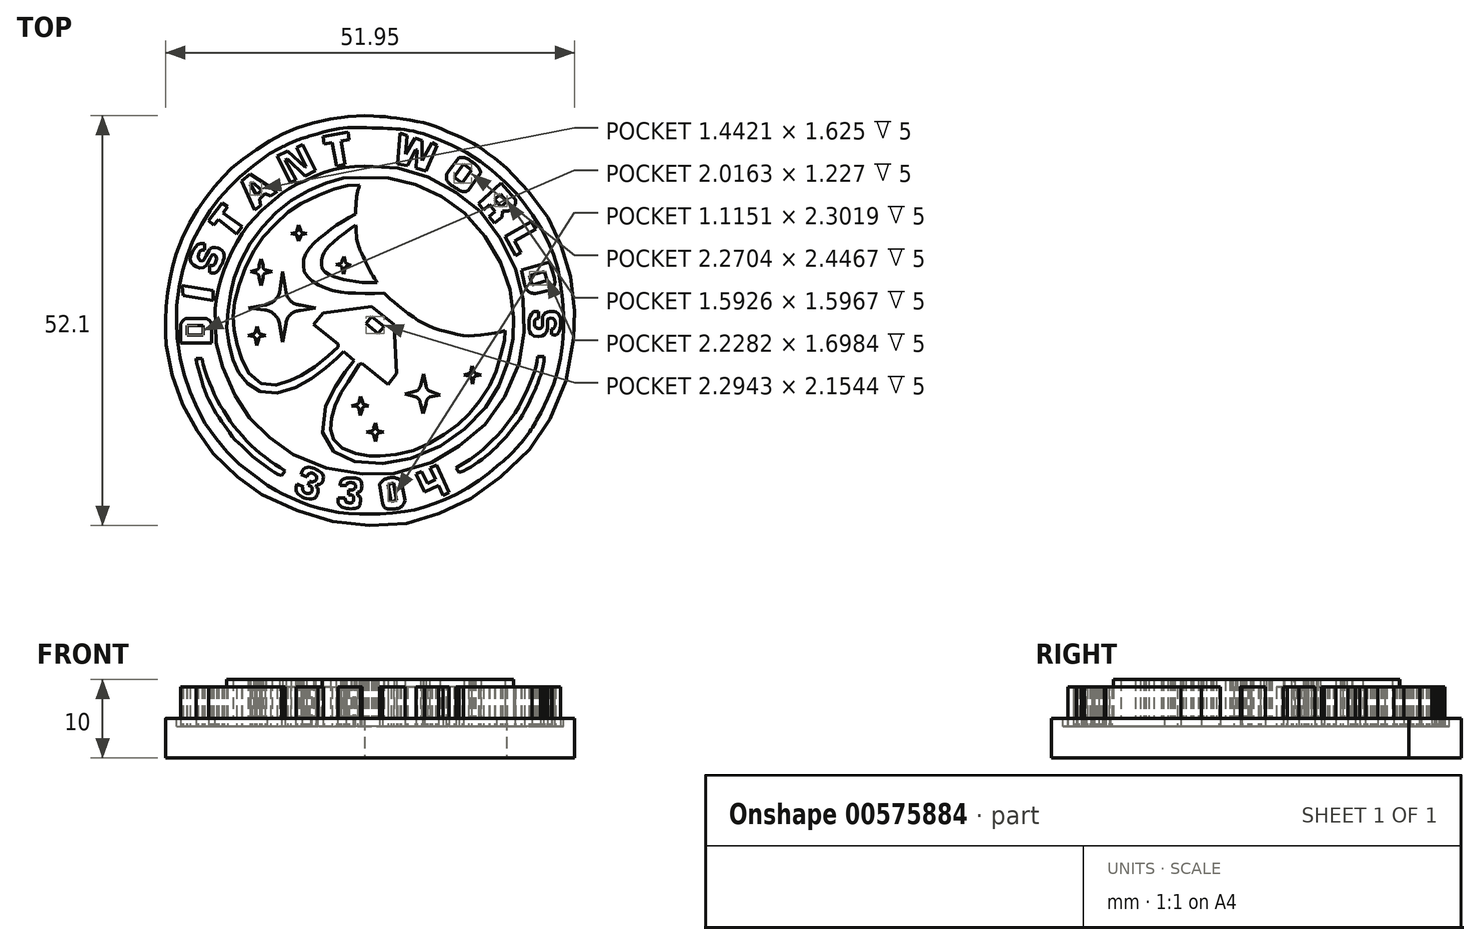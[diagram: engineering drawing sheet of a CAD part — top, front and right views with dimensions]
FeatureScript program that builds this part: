
annotation { "Feature Type Name" : "Feature", "Feature Type Description" : "" }
export const myFeature = defineFeature(function(context is Context, id is Id, definition is map)
    precondition{}
    {
        {
            var Q0;
            Q0=qCreatedBy(makeId("Top.planeOp"),FACE);
            var sketch = newSketch(context, id + "F0", { "sketchPlane" : qUnion([Q0])});
            skFitSpline(sketch, "E0", {"points": [v(33.66, 54.7) * mm, v(28.64, 54.13) * mm, v(24.15, 52.76) * mm, v(20.9, 51.03) * mm, v(17.39, 48.57) * mm, v(15.5, 46.67) * mm, v(13.56, 44.31) * mm, v(11.47, 41.1) * mm, v(9.64, 36.9) * mm, v(9.01, 34.3) * mm, v(8.48, 31.08) * mm, v(8.38, 27.96) * mm, v(8.48, 25.57) * mm], "startDerivative": vector(-44.63, -0.28) * mm, "endDerivative": vector(4.64, -29.37) * mm});
            skFitSpline(sketch, "E1", {"points": [v(8.48, 25.57) * mm, v(9.04, 22.5) * mm, v(9.97, 19.28) * mm, v(11.27, 16.56) * mm, v(12.7, 14.13) * mm, v(14.12, 12.14) * mm, v(16.89, 9.38) * mm, v(19.17, 7.53) * mm, v(22.3, 5.7) * mm, v(27.48, 3.7) * mm, v(31.2, 2.9) * mm, v(36.42, 2.6) * mm, v(40.28, 3.17) * mm, v(43.93, 4.47) * mm, v(47.72, 6.36) * mm, v(51.35, 9.16) * mm, v(55.07, 12.81) * mm, v(57.46, 16.57) * mm, v(59.59, 22.19) * mm, v(60.29, 27.4) * mm, v(60.32, 29.57) * mm, v(59.95, 33.52) * mm, v(59.06, 36.85) * mm, v(57.9, 40.04) * mm, v(56.33, 42.66) * mm, v(54.07, 45.62) * mm, v(51.71, 48.05) * mm], "startDerivative": vector(14.51, -87.06) * mm, "endDerivative": vector(-72.64, 61.42) * mm});
            skFitSpline(sketch, "E2", {"points": [v(51.71, 48.05) * mm, v(48.99, 50.18) * mm, v(47.02, 51.4) * mm, v(44.2, 52.67) * mm, v(41.74, 53.63) * mm, v(38.88, 54.2) * mm, v(36.42, 54.53) * mm, v(33.66, 54.7) * mm], "startDerivative": vector(-17.82, 14.28) * mm, "endDerivative": vector(-30.74, 1.43) * mm});
            skSolve(sketch);
        }
        {
            var Q0;
            Q0 = qSketchRegion(id + "F0", true);
            extrude(context, id + "F1", {"entities" : qUnion([Q0]), "depth" : 5 * mm, "offsetDistance" : 25 * mm});
        }
        {
            var Q0;
            Q0=makeQuery(id+"F1.opExtrude","CAP_FACE",FACE,{"disambiguationData":[OSD([sQuery(id+"F0.wireOp",EDGE,"E0"),sQuery(id+"F0.wireOp",EDGE,"E1"),sQuery(id+"F0.wireOp",EDGE,"E2")])],"isStart":false});
            var sketch = newSketch(context, id + "F2", { "sketchPlane" : qUnion([Q0])});
            skFitSpline(sketch, "E3", {"points": [v(26.87, 52.15) * mm, v(24.92, 51.5) * mm, v(23.24, 50.73) * mm, v(21.37, 49.7) * mm], "startDerivative": vector(-6, -1.7) * mm, "endDerivative": vector(-5.43, -3.28) * mm});
            skFitSpline(sketch, "E4", {"points": [v(21.37, 49.7) * mm, v(20.03, 48.73) * mm, v(18.51, 47.52) * mm, v(17.4, 46.52) * mm, v(16.7, 45.8) * mm, v(15.56, 44.58) * mm, v(14.8, 43.75) * mm, v(14.16, 42.85) * mm, v(13.55, 41.87) * mm, v(12.56, 40.19) * mm, v(11.73, 38.52) * mm, v(11.22, 37.14) * mm, v(10.85, 35.97) * mm, v(10.46, 34.7) * mm, v(10.18, 33.2) * mm, v(9.83, 31.07) * mm, v(9.81, 29.8) * mm, v(9.79, 28.26) * mm, v(9.83, 26.76) * mm, v(10.11, 24.62) * mm, v(10.52, 22.74) * mm, v(10.87, 21.34) * mm, v(11.56, 19.44) * mm, v(12.34, 17.62) * mm, v(12.97, 16.39) * mm, v(13.92, 14.83) * mm, v(15.02, 13.43) * mm, v(16.07, 12.14) * mm, v(17.25, 10.88) * mm, v(18.36, 9.98) * mm, v(19.84, 8.78) * mm, v(21.37, 7.7) * mm], "startDerivative": vector(-43.18, -27.56) * mm, "endDerivative": vector(47.9, -24.44) * mm});
            skFitSpline(sketch, "E5", {"points": [v(21.37, 7.7) * mm, v(22.62, 6.94) * mm, v(23.33, 6.6) * mm, v(24.66, 6) * mm, v(26.33, 5.3) * mm, v(27.53, 4.89) * mm, v(29.48, 4.45) * mm, v(30.91, 4.22) * mm, v(32.77, 4.13) * mm, v(34.37, 4.1) * mm, v(36.53, 4.14) * mm, v(38.97, 4.43) * mm, v(40.53, 4.74) * mm, v(42.3, 5.3) * mm, v(44.22, 6.09) * mm, v(46.5, 7.23) * mm, v(49.04, 8.94) * mm, v(50.5, 10.16) * mm], "startDerivative": vector(25.71, -16.24) * mm, "endDerivative": vector(21.37, 21.4) * mm});
            skFitSpline(sketch, "E6", {"points": [v(50.5, 10.16) * mm, v(52.82, 12.29) * mm, v(54.13, 13.87) * mm, v(55.07, 15.18) * mm, v(56.1, 17.01) * mm], "startDerivative": vector(8.33, 7.24) * mm, "endDerivative": vector(4.94, 7.57) * mm});
            skFitSpline(sketch, "E7", {"points": [v(56.1, 17.01) * mm, v(57.07, 19.1) * mm, v(57.9, 21.27) * mm, v(58.38, 23.01) * mm, v(58.74, 25.12) * mm, v(58.9, 27.05) * mm, v(58.96, 29.28) * mm, v(58.76, 31.76) * mm, v(58.42, 34.2) * mm, v(57.83, 36.57) * mm, v(57.05, 38.48) * mm, v(56.1, 40.32) * mm, v(54.62, 42.64) * mm, v(53.36, 44.28) * mm, v(52.3, 45.5) * mm, v(49.9, 47.68) * mm, v(48.22, 48.99) * mm, v(45.67, 50.48) * mm, v(43.38, 51.55) * mm, v(41.07, 52.42) * mm], "startDerivative": vector(18.57, 39) * mm, "endDerivative": vector(-43.4, 12.3) * mm});
            skFitSpline(sketch, "E8", {"points": [v(41.07, 52.42) * mm, v(39.18, 52.84) * mm, v(37.64, 53) * mm, v(35.9, 53.11) * mm, v(33.42, 53.15) * mm, v(31.55, 53.15) * mm, v(29.82, 52.95) * mm, v(26.87, 52.15) * mm], "startDerivative": vector(-13.88, 3.44) * mm, "endDerivative": vector(-17.96, -5.4) * mm});
            skFitSpline(sketch, "E9", {"points": [v(33.66, 48.3) * mm, v(30.82, 48.08) * mm, v(27.92, 47.23) * mm, v(25.62, 46.22) * mm, v(23.66, 45.18) * mm, v(22.01, 43.86) * mm, v(20.42, 42.46) * mm, v(18.59, 40.38) * mm, v(17.12, 38.06) * mm, v(15.96, 35.52) * mm, v(15.16, 33.13) * mm, v(14.7, 30.17) * mm], "startDerivative": vector(-29.66, -0.71) * mm, "endDerivative": vector(-1.88, -34.71) * mm});
            skFitSpline(sketch, "E10", {"points": [v(14.7, 30.17) * mm, v(14.7, 26.26) * mm, v(15.2, 24.08) * mm, v(15.8, 22.28) * mm, v(17.12, 19.38) * mm, v(18.2, 17.48) * mm, v(19.75, 15.5) * mm, v(21.46, 13.94) * mm, v(23.39, 12.32) * mm, v(26.35, 10.85) * mm, v(30.66, 9.41) * mm, v(34.55, 9.14) * mm, v(37.51, 9.23) * mm, v(42.25, 10.66) * mm, v(44.97, 12.22) * mm, v(47.78, 14.33) * mm, v(50.29, 17) * mm, v(52.03, 20.2) * mm, v(53.53, 24.12) * mm, v(53.93, 27.14) * mm, v(53.9, 30.72) * mm, v(53.35, 33.47) * mm, v(52.19, 36.83) * mm, v(50.29, 40.04) * mm, v(48.24, 42.61) * mm, v(45.89, 44.5) * mm, v(43.32, 46.16) * mm, v(40.14, 47.5) * mm, v(37.33, 48.11) * mm, v(33.66, 48.3) * mm], "startDerivative": vector(-5, -110.22) * mm, "endDerivative": vector(-103.89, 2.26) * mm});
            skSolve(sketch);
        }
        {
            var Q0;
            Q0 = qSketchRegion(id + "F2", true);
            extrude(context, id + "F3", {"entities" : qUnion([Q0]), "operationType" : NewBodyOperationType.REMOVE, "oppositeDirection" : true, "depth" : 1 * mm, "offsetDistance" : 25 * mm});
        }
        {
            var Q0;
            Q0=makeQuery(id+"F3.boolean.opBoolean","COPY",FACE,{"derivedFrom":makeQuery(id+"F3.opExtrude","CAP_FACE",FACE,{"disambiguationData":[OSD([sQuery(id+"F2.wireOp",EDGE,"E3"),sQuery(id+"F2.wireOp",EDGE,"E4"),sQuery(id+"F2.wireOp",EDGE,"E5"),sQuery(id+"F2.wireOp",EDGE,"E6"),sQuery(id+"F2.wireOp",EDGE,"E7"),sQuery(id+"F2.wireOp",EDGE,"E8"),sQuery(id+"F2.wireOp",EDGE,"E9"),sQuery(id+"F2.wireOp",EDGE,"E10")])],"isStart":false})});
            var sketch = newSketch(context, id + "F4", { "sketchPlane" : qUnion([Q0])});
            skLineSegment(sketch, "E11", {"start": v(31.56, 52.63) * mm, "end": v(28.37, 52.04) * mm});
            skLineSegment(sketch, "E12", {"start": v(28.37, 52.04) * mm, "end": v(28.54, 51.1) * mm});
            skLineSegment(sketch, "E13", {"start": v(28.54, 51.1) * mm, "end": v(29.55, 51.28) * mm});
            skLineSegment(sketch, "E14", {"start": v(29.55, 51.28) * mm, "end": v(30.1, 48.3) * mm});
            skLineSegment(sketch, "E15", {"start": v(30.1, 48.3) * mm, "end": v(31.2, 48.5) * mm});
            skLineSegment(sketch, "E16", {"start": v(31.2, 48.5) * mm, "end": v(30.66, 51.48) * mm});
            skLineSegment(sketch, "E17", {"start": v(30.66, 51.48) * mm, "end": v(31.7, 51.67) * mm});
            skLineSegment(sketch, "E18", {"start": v(31.56, 52.63) * mm, "end": v(31.7, 51.67) * mm});
            skLineSegment(sketch, "E19", {"start": v(24.95, 46.52) * mm, "end": v(24.28, 46.17) * mm});
            skLineSegment(sketch, "E20", {"start": v(24.28, 46.17) * mm, "end": v(22.54, 49.54) * mm});
            skLineSegment(sketch, "E21", {"start": v(22.54, 49.54) * mm, "end": v(23.85, 50.21) * mm});
            skLineSegment(sketch, "E22", {"start": v(23.85, 50.21) * mm, "end": v(26.08, 48.14) * mm});
            skLineSegment(sketch, "E23", {"start": v(26.25, 48.24) * mm, "end": v(25.03, 50.62) * mm});
            skLineSegment(sketch, "E24", {"start": v(25.03, 50.62) * mm, "end": v(25.78, 51) * mm});
            skLineSegment(sketch, "E25", {"start": v(25.78, 51) * mm, "end": v(27.46, 47.73) * mm});
            skLineSegment(sketch, "E26", {"start": v(27.46, 47.73) * mm, "end": v(26.08, 47.02) * mm});
            skLineSegment(sketch, "E27", {"start": v(26.08, 47.02) * mm, "end": v(23.86, 49.15) * mm});
            skLineSegment(sketch, "E28", {"start": v(23.6, 49.03) * mm, "end": v(24.95, 46.52) * mm});
            skLineSegment(sketch, "E29", {"start": v(23.86, 49.15) * mm, "end": v(23.6, 49.03) * mm});
            skLineSegment(sketch, "E30", {"start": v(26.25, 48.24) * mm, "end": v(26.08, 48.14) * mm});
            skLineSegment(sketch, "E31", {"start": v(19.12, 47.29) * mm, "end": v(18.07, 46.38) * mm});
            skLineSegment(sketch, "E32", {"start": v(18.07, 46.38) * mm, "end": v(19.66, 42.68) * mm});
            skLineSegment(sketch, "E33", {"start": v(19.66, 42.68) * mm, "end": v(20.48, 43.28) * mm});
            skLineSegment(sketch, "E34", {"start": v(20.48, 43.28) * mm, "end": v(20.32, 44.1) * mm});
            skLineSegment(sketch, "E35", {"start": v(20.32, 44.1) * mm, "end": v(21.02, 44.79) * mm});
            skLineSegment(sketch, "E36", {"start": v(21.02, 44.79) * mm, "end": v(21.74, 44.5) * mm});
            skLineSegment(sketch, "E37", {"start": v(21.74, 44.5) * mm, "end": v(22.53, 45.06) * mm});
            skLineSegment(sketch, "E38", {"start": v(22.53, 45.06) * mm, "end": v(19.12, 47.29) * mm});
            skLineSegment(sketch, "E39", {"start": v(19.36, 46.25) * mm, "end": v(20.56, 45.26) * mm});
            skLineSegment(sketch, "E40", {"start": v(20.56, 45.26) * mm, "end": v(19.92, 44.63) * mm});
            skLineSegment(sketch, "E41", {"start": v(19.92, 44.63) * mm, "end": v(19.12, 46) * mm});
            skLineSegment(sketch, "E42", {"start": v(19.36, 46.25) * mm, "end": v(19.12, 46) * mm});
            skLineSegment(sketch, "E43", {"start": v(15.57, 43.62) * mm, "end": v(13.85, 41.36) * mm});
            skLineSegment(sketch, "E44", {"start": v(13.85, 41.36) * mm, "end": v(14.46, 40.8) * mm});
            skLineSegment(sketch, "E45", {"start": v(14.46, 40.8) * mm, "end": v(15.1, 41.5) * mm});
            skLineSegment(sketch, "E46", {"start": v(15.1, 41.5) * mm, "end": v(17.38, 39.67) * mm});
            skLineSegment(sketch, "E47", {"start": v(17.38, 39.67) * mm, "end": v(18.12, 40.58) * mm});
            skLineSegment(sketch, "E48", {"start": v(18.12, 40.58) * mm, "end": v(15.67, 42.33) * mm});
            skLineSegment(sketch, "E49", {"start": v(15.57, 43.62) * mm, "end": v(16.23, 43.11) * mm});
            skLineSegment(sketch, "E50", {"start": v(16.23, 43.11) * mm, "end": v(15.67, 42.33) * mm});
            skFitSpline(sketch, "E51", {"points": [v(13.33, 38.46) * mm, v(12.7, 38.42) * mm, v(12.38, 38.23) * mm, v(12.09, 37.85) * mm, v(11.83, 37.44) * mm, v(11.6, 36.9) * mm, v(11.52, 36.37) * mm, v(11.65, 36.02) * mm, v(11.97, 35.68) * mm, v(12.4, 35.45) * mm, v(13, 35.3) * mm, v(13.61, 35.76) * mm, v(13.95, 36.3) * mm, v(14.2, 36.9) * mm, v(14.4, 37.03) * mm, v(14.65, 37) * mm, v(14.87, 36.74) * mm, v(14.86, 36.43) * mm, v(14.73, 36.01) * mm, v(14.56, 35.74) * mm, v(14.33, 35.65) * mm, v(13.98, 35.65) * mm], "startDerivative": vector(-10.58, 1.4) * mm, "endDerivative": vector(-5.63, -0.2) * mm});
            skLineSegment(sketch, "E52", {"start": v(13.98, 35.65) * mm, "end": v(13.98, 34.78) * mm});
            skLineSegment(sketch, "E53", {"start": v(13.33, 38.46) * mm, "end": v(13.33, 37.64) * mm});
            skFitSpline(sketch, "E54", {"points": [v(13.98, 34.78) * mm, v(14.78, 34.78) * mm, v(15.3, 35.41) * mm, v(15.46, 35.71) * mm, v(15.71, 36.3) * mm], "startDerivative": vector(2.67, -0.65) * mm, "endDerivative": vector(0.47, 2.65) * mm});
            skFitSpline(sketch, "E55", {"points": [v(15.71, 36.3) * mm, v(15.83, 36.86) * mm, v(15.71, 37.44) * mm, v(15.3, 37.76) * mm, v(14.8, 37.92) * mm, v(14.2, 37.9) * mm, v(13.88, 37.55) * mm, v(13.58, 36.97) * mm, v(13.38, 36.57) * mm, v(13.13, 36.27) * mm, v(12.77, 36.3) * mm, v(12.58, 36.6) * mm, v(12.54, 36.98) * mm, v(12.69, 37.4) * mm, v(12.91, 37.57) * mm, v(13.33, 37.64) * mm], "startDerivative": vector(3.34, 6.88) * mm, "endDerivative": vector(6.34, 0.42) * mm});
            skLineSegment(sketch, "E56", {"start": v(10.48, 33.1) * mm, "end": v(14.43, 32.49) * mm});
            skLineSegment(sketch, "E57", {"start": v(14.43, 32.49) * mm, "end": v(14.43, 31.22) * mm});
            skLineSegment(sketch, "E58", {"start": v(14.43, 31.22) * mm, "end": v(10.59, 31.85) * mm});
            skLineSegment(sketch, "E59", {"start": v(10.59, 31.85) * mm, "end": v(10.48, 33.1) * mm});
            skLineSegment(sketch, "E60", {"start": v(10.28, 25.8) * mm, "end": v(14.25, 25.8) * mm});
            skLineSegment(sketch, "E61", {"start": v(14.25, 25.8) * mm, "end": v(14.25, 28) * mm});
            skLineSegment(sketch, "E62", {"start": v(10.28, 25.8) * mm, "end": v(10.28, 28) * mm});
            skLineSegment(sketch, "E63", {"start": v(11.02, 28.95) * mm, "end": v(13.27, 28.95) * mm});
            skFitSpline(sketch, "E64", {"points": [v(11.02, 28.95) * mm, v(10.78, 28.82) * mm, v(10.57, 28.64) * mm, v(10.41, 28.43) * mm, v(10.32, 28.24) * mm, v(10.28, 28) * mm], "startDerivative": vector(-1.22, -0.54) * mm, "endDerivative": vector(-0.17, -1.31) * mm});
            skFitSpline(sketch, "E65", {"points": [v(13.27, 28.95) * mm, v(13.56, 28.9) * mm, v(13.8, 28.8) * mm, v(14.05, 28.58) * mm, v(14.2, 28.27) * mm, v(14.25, 28) * mm], "startDerivative": vector(1.5, -0.14) * mm, "endDerivative": vector(0.37, -1.17) * mm});
            skLineSegment(sketch, "E66", {"start": v(11.14, 28.04) * mm, "end": v(13.16, 28.04) * mm});
            skLineSegment(sketch, "E67", {"start": v(13.16, 28.04) * mm, "end": v(13.16, 26.81) * mm});
            skLineSegment(sketch, "E68", {"start": v(13.16, 26.81) * mm, "end": v(11.14, 26.81) * mm});
            skLineSegment(sketch, "E69", {"start": v(11.14, 26.81) * mm, "end": v(11.14, 28.04) * mm});
            skLineSegment(sketch, "E70", {"start": v(12.26, 23.87) * mm, "end": v(13.03, 23.87) * mm});
            skLineSegment(sketch, "E71", {"start": v(23.55, 9.56) * mm, "end": v(23.13, 8.97) * mm});
            skFitSpline(sketch, "E72", {"points": [v(13.03, 23.87) * mm, v(13.3, 22.54) * mm, v(13.83, 21.12) * mm, v(14.26, 20.07) * mm, v(14.82, 18.81) * mm, v(15.46, 17.68) * mm, v(16.2, 16.56) * mm, v(16.78, 15.58) * mm, v(17.78, 14.4) * mm, v(18.7, 13.35) * mm, v(19.64, 12.43) * mm, v(20.42, 11.79) * mm, v(21.62, 10.85) * mm, v(22.54, 10.25) * mm, v(23.55, 9.56) * mm], "startDerivative": vector(2.92, -17.86) * mm, "endDerivative": vector(14.98, -10.3) * mm});
            skFitSpline(sketch, "E73", {"points": [v(12.26, 23.87) * mm, v(12.43, 22.83) * mm, v(12.8, 21.63) * mm, v(13.19, 20.26) * mm, v(13.86, 18.64) * mm], "startDerivative": vector(0.51, -4.64) * mm, "endDerivative": vector(3.07, -5.4) * mm});
            skFitSpline(sketch, "E74", {"points": [v(13.86, 18.64) * mm, v(14.66, 17.1) * mm, v(15.55, 15.76) * mm, v(16.27, 14.78) * mm, v(17.07, 13.68) * mm, v(18.03, 12.75) * mm, v(19.12, 11.68) * mm, v(20.33, 10.7) * mm, v(21.42, 9.94) * mm, v(22.31, 9.31) * mm, v(23.13, 8.97) * mm], "startDerivative": vector(6.74, -13.78) * mm, "endDerivative": vector(10.2, -3.58) * mm});
            skLineSegment(sketch, "E75", {"start": v(26.34, 8.77) * mm, "end": v(25.58, 9.13) * mm});
            skLineSegment(sketch, "E76", {"start": v(25.09, 7.91) * mm, "end": v(25.89, 7.54) * mm});
            skFitSpline(sketch, "E77", {"points": [v(25.58, 9.13) * mm, v(25.86, 9.74) * mm, v(26.36, 10.02) * mm, v(26.9, 10) * mm, v(27.56, 9.71) * mm, v(28.09, 9.42) * mm, v(28.4, 9) * mm, v(28.4, 8.52) * mm, v(28.23, 8.02) * mm, v(27.85, 7.83) * mm, v(27.65, 7.83) * mm], "startDerivative": vector(1.82, 5.93) * mm, "endDerivative": vector(-2.85, 0.29) * mm});
            skLineSegment(sketch, "E78", {"start": v(27.65, 7.83) * mm, "end": v(27.5, 7.5) * mm});
            skFitSpline(sketch, "E79", {"points": [v(27.5, 7.5) * mm, v(27.75, 7.33) * mm, v(27.76, 6.96) * mm, v(27.62, 6.53) * mm, v(27.42, 6.16) * mm, v(27.07, 6.03) * mm, v(26.1, 6.08) * mm, v(25.47, 6.43) * mm, v(25.13, 6.73) * mm, v(24.98, 7.08) * mm, v(24.99, 7.57) * mm, v(25.09, 7.91) * mm], "startDerivative": vector(4.2, -1.78) * mm, "endDerivative": vector(1.45, 4) * mm});
            skFitSpline(sketch, "E80", {"points": [v(25.89, 7.54) * mm, v(25.77, 7.3) * mm, v(25.89, 6.98) * mm, v(26.1, 6.8) * mm, v(26.51, 6.7) * mm, v(26.86, 6.78) * mm, v(26.98, 7.01) * mm, v(26.96, 7.4) * mm, v(26.8, 7.63) * mm, v(26.5, 7.72) * mm], "startDerivative": vector(-1.61, -2.16) * mm, "endDerivative": vector(-3.26, 0.4) * mm});
            skLineSegment(sketch, "E81", {"start": v(26.5, 7.72) * mm, "end": v(26.67, 8.24) * mm});
            skFitSpline(sketch, "E82", {"points": [v(26.67, 8.24) * mm, v(27.04, 8.17) * mm, v(27.49, 8.37) * mm, v(27.58, 8.73) * mm, v(27.36, 9.08) * mm, v(26.91, 9.3) * mm, v(26.67, 9.25) * mm, v(26.42, 9.04) * mm, v(26.34, 8.77) * mm], "startDerivative": vector(2.73, -1) * mm, "endDerivative": vector(-0.4, -2.54) * mm});
            skLineSegment(sketch, "E83", {"start": v(30.56, 7.7) * mm, "end": v(31.4, 7.7) * mm});
            skLineSegment(sketch, "E84", {"start": v(30.3, 6.13) * mm, "end": v(31.2, 6.13) * mm});
            skLineSegment(sketch, "E85", {"start": v(31.64, 7.17) * mm, "end": v(31.64, 6.53) * mm});
            skLineSegment(sketch, "E86", {"start": v(32.77, 6.9) * mm, "end": v(32.77, 6.46) * mm});
            skFitSpline(sketch, "E87", {"points": [v(30.56, 7.7) * mm, v(30.67, 8.28) * mm, v(31.02, 8.54) * mm], "startDerivative": vector(0.05, 1.21) * mm, "endDerivative": vector(0.88, 0.45) * mm});
            skFitSpline(sketch, "E88", {"points": [v(31.02, 8.54) * mm, v(31.53, 8.68) * mm, v(32.1, 8.68) * mm, v(32.63, 8.65) * mm, v(33.04, 8.43) * mm, v(33.25, 8.12) * mm, v(33.31, 7.58) * mm, v(33.25, 7.13) * mm, v(33.11, 6.96) * mm, v(32.77, 6.9) * mm], "startDerivative": vector(4.2, 1.44) * mm, "endDerivative": vector(-4.17, 0.7) * mm});
            skFitSpline(sketch, "E89", {"points": [v(32.77, 6.46) * mm, v(33.06, 6.28) * mm, v(33.12, 5.72) * mm, v(33.04, 5.2) * mm, v(32.77, 4.88) * mm, v(32.4, 4.78) * mm, v(31.7, 4.76) * mm, v(31.17, 4.84) * mm, v(30.75, 5.01) * mm, v(30.38, 5.33) * mm, v(30.3, 5.6) * mm, v(30.3, 6.13) * mm], "startDerivative": vector(4.43, -1.64) * mm, "endDerivative": vector(1.3, 6.07) * mm});
            skFitSpline(sketch, "E90", {"points": [v(31.2, 6.13) * mm, v(31.3, 5.62) * mm, v(31.7, 5.5) * mm, v(32.13, 5.56) * mm, v(32.26, 5.9) * mm, v(32.25, 6.22) * mm, v(32.12, 6.48) * mm, v(31.64, 6.53) * mm], "startDerivative": vector(0.04, -3.73) * mm, "endDerivative": vector(-3.61, -0.18) * mm});
            skFitSpline(sketch, "E91", {"points": [v(31.64, 7.17) * mm, v(32.22, 7.17) * mm, v(32.48, 7.4) * mm, v(32.52, 7.7) * mm, v(32.34, 7.96) * mm, v(31.94, 8.09) * mm, v(31.64, 8.03) * mm, v(31.4, 7.93) * mm, v(31.4, 7.7) * mm], "startDerivative": vector(3.86, -0.46) * mm, "endDerivative": vector(0.52, -2.5) * mm});
            skLineSegment(sketch, "E92", {"start": v(35.57, 7.84) * mm, "end": v(35.94, 5.43) * mm});
            skLineSegment(sketch, "E93", {"start": v(36.64, 7.87) * mm, "end": v(37.34, 8) * mm});
            skLineSegment(sketch, "E94", {"start": v(37.34, 8) * mm, "end": v(37.76, 5.84) * mm});
            skLineSegment(sketch, "E95", {"start": v(37.76, 5.84) * mm, "end": v(37.05, 5.7) * mm});
            skLineSegment(sketch, "E96", {"start": v(37.05, 5.7) * mm, "end": v(36.64, 7.87) * mm});
            skLineSegment(sketch, "E97", {"start": v(38.3, 8.36) * mm, "end": v(38.8, 5.8) * mm});
            skFitSpline(sketch, "E98", {"points": [v(35.57, 7.84) * mm, v(36.05, 8.4) * mm, v(36.58, 8.61) * mm, v(37.24, 8.73) * mm, v(37.77, 8.6) * mm, v(38.3, 8.36) * mm], "startDerivative": vector(2.08, 2.92) * mm, "endDerivative": vector(2.76, -1.28) * mm});
            skFitSpline(sketch, "E99", {"points": [v(38.8, 5.8) * mm, v(38.43, 5.1) * mm, v(37.58, 4.74) * mm, v(36.8, 4.74) * mm, v(36.24, 4.86) * mm, v(35.94, 5.43) * mm], "startDerivative": vector(-1.28, -3.68) * mm, "endDerivative": vector(-1.98, 3.17) * mm});
            skLineSegment(sketch, "E100", {"start": v(45.28, 9.95) * mm, "end": v(45.67, 9.34) * mm});
            skLineSegment(sketch, "E101", {"start": v(55.6, 24.09) * mm, "end": v(56.43, 24.09) * mm});
            skFitSpline(sketch, "E102", {"points": [v(56.43, 24.09) * mm, v(56.43, 23.39) * mm, v(56.24, 22.49) * mm, v(56, 21.7) * mm], "startDerivative": vector(0.1, -2.14) * mm, "endDerivative": vector(-1.08, -1.99) * mm});
            skFitSpline(sketch, "E103", {"points": [v(56, 21.7) * mm, v(55.69, 20.78) * mm, v(54.94, 19.05) * mm], "startDerivative": vector(-0.7, -1.88) * mm, "endDerivative": vector(-1.3, -2.78) * mm});
            skFitSpline(sketch, "E104", {"points": [v(54.94, 19.05) * mm, v(54.51, 18.1) * mm, v(54.12, 17.36) * mm, v(53.6, 16.45) * mm, v(52.83, 15.37) * mm, v(52.24, 14.64) * mm, v(51.62, 13.85) * mm, v(50.72, 12.9) * mm, v(49.84, 12.08) * mm, v(48.87, 11.25) * mm, v(47.9, 10.58) * mm, v(47.1, 10.05) * mm, v(46.22, 9.54) * mm], "startDerivative": vector(-5.34, -12.08) * mm, "endDerivative": vector(-11.37, -6.03) * mm});
            skLineSegment(sketch, "E105", {"start": v(46.22, 9.54) * mm, "end": v(45.67, 9.34) * mm});
            skFitSpline(sketch, "E106", {"points": [v(45.28, 9.95) * mm, v(46.02, 10.4) * mm, v(47, 11.01) * mm, v(47.7, 11.5) * mm, v(48.56, 12.16) * mm, v(49.59, 13.14) * mm, v(50.7, 14.2) * mm, v(51.83, 15.62) * mm, v(52.95, 17.16) * mm, v(53.81, 18.82) * mm, v(54.36, 19.9) * mm, v(54.9, 21.2) * mm, v(55.31, 22.32) * mm, v(55.51, 23.19) * mm, v(55.6, 24.09) * mm], "startDerivative": vector(11.87, 7.35) * mm, "endDerivative": vector(0.88, 16) * mm});
            skLineSegment(sketch, "E107", {"start": v(38.14, 52.46) * mm, "end": v(39.05, 52.18) * mm});
            skLineSegment(sketch, "E108", {"start": v(39.05, 52.18) * mm, "end": v(38.9, 49.8) * mm});
            skLineSegment(sketch, "E109", {"start": v(38.9, 49.8) * mm, "end": v(40.09, 51.86) * mm});
            skLineSegment(sketch, "E110", {"start": v(40.09, 51.86) * mm, "end": v(40.98, 51.52) * mm});
            skLineSegment(sketch, "E111", {"start": v(40.98, 51.52) * mm, "end": v(40.98, 48.97) * mm});
            skLineSegment(sketch, "E112", {"start": v(40.98, 48.97) * mm, "end": v(42.2, 51.28) * mm});
            skLineSegment(sketch, "E113", {"start": v(42.2, 51.28) * mm, "end": v(42.89, 50.91) * mm});
            skLineSegment(sketch, "E114", {"start": v(42.89, 50.91) * mm, "end": v(41.45, 47.63) * mm});
            skLineSegment(sketch, "E115", {"start": v(41.45, 47.63) * mm, "end": v(40.23, 48) * mm});
            skLineSegment(sketch, "E116", {"start": v(40.23, 48) * mm, "end": v(40.32, 50.34) * mm});
            skLineSegment(sketch, "E117", {"start": v(40.1, 50.4) * mm, "end": v(39.13, 48.38) * mm});
            skLineSegment(sketch, "E118", {"start": v(39.13, 48.38) * mm, "end": v(37.87, 48.57) * mm});
            skLineSegment(sketch, "E119", {"start": v(37.87, 48.57) * mm, "end": v(38.14, 52.46) * mm});
            skLineSegment(sketch, "E120", {"start": v(40.1, 50.4) * mm, "end": v(40.32, 50.34) * mm});
            skLineSegment(sketch, "E121", {"start": v(46.26, 48.55) * mm, "end": v(47.27, 47.76) * mm});
            skLineSegment(sketch, "E122", {"start": v(47.27, 47.76) * mm, "end": v(46.05, 46.1) * mm});
            skLineSegment(sketch, "E123", {"start": v(46.05, 46.1) * mm, "end": v(45, 46.88) * mm});
            skLineSegment(sketch, "E124", {"start": v(46.26, 48.55) * mm, "end": v(45, 46.88) * mm});
            skLineSegment(sketch, "E125", {"start": v(45.68, 49.37) * mm, "end": v(44.2, 47.45) * mm});
            skLineSegment(sketch, "E126", {"start": v(48.4, 47.38) * mm, "end": v(46.9, 45.25) * mm});
            skFitSpline(sketch, "E127", {"points": [v(45.68, 49.37) * mm, v(46.38, 49.37) * mm, v(46.88, 49.1) * mm, v(47.31, 48.84) * mm, v(47.8, 48.46) * mm, v(48.2, 47.95) * mm, v(48.4, 47.38) * mm], "startDerivative": vector(4.05, 0.45) * mm, "endDerivative": vector(0.94, -5.11) * mm});
            skFitSpline(sketch, "E128", {"points": [v(46.9, 45.25) * mm, v(46.34, 45.02) * mm, v(45.63, 45.25) * mm], "startDerivative": vector(-1.22, -0.83) * mm, "endDerivative": vector(-1.36, 0.82) * mm});
            skFitSpline(sketch, "E129", {"points": [v(45.63, 45.25) * mm, v(44.92, 45.7) * mm, v(44.32, 46.17) * mm, v(44.1, 46.62) * mm, v(44.11, 47.24) * mm, v(44.2, 47.45) * mm], "startDerivative": vector(-2.95, 1.69) * mm, "endDerivative": vector(0.43, 1.35) * mm});
            skLineSegment(sketch, "E130", {"start": v(50.97, 46.1) * mm, "end": v(48.13, 43.5) * mm});
            skLineSegment(sketch, "E131", {"start": v(48.13, 43.5) * mm, "end": v(48.75, 42.73) * mm});
            skLineSegment(sketch, "E132", {"start": v(48.75, 42.73) * mm, "end": v(49.55, 43.38) * mm});
            skLineSegment(sketch, "E133", {"start": v(49.55, 43.38) * mm, "end": v(50.26, 42.5) * mm});
            skLineSegment(sketch, "E134", {"start": v(50.26, 42.5) * mm, "end": v(49.48, 41.87) * mm});
            skLineSegment(sketch, "E135", {"start": v(49.48, 41.87) * mm, "end": v(50.17, 41.02) * mm});
            skLineSegment(sketch, "E136", {"start": v(50.17, 41.02) * mm, "end": v(51.15, 41.82) * mm});
            skLineSegment(sketch, "E137", {"start": v(50.97, 46.1) * mm, "end": v(52.78, 44.1) * mm});
            skFitSpline(sketch, "E138", {"points": [v(52.78, 44.1) * mm, v(52.78, 43.35) * mm, v(52.23, 42.75) * mm, v(51.84, 42.57) * mm, v(51.18, 42.55) * mm], "startDerivative": vector(0.6, -2.95) * mm, "endDerivative": vector(-2.79, 0.14) * mm});
            skLineSegment(sketch, "E139", {"start": v(51.18, 42.55) * mm, "end": v(51.15, 41.82) * mm});
            skLineSegment(sketch, "E140", {"start": v(50.95, 44.71) * mm, "end": v(50.19, 44.04) * mm});
            skLineSegment(sketch, "E141", {"start": v(50.19, 44.04) * mm, "end": v(51, 43.12) * mm});
            skLineSegment(sketch, "E142", {"start": v(51, 43.12) * mm, "end": v(51.78, 43.8) * mm});
            skLineSegment(sketch, "E143", {"start": v(51.78, 43.8) * mm, "end": v(50.95, 44.71) * mm});
            skLineSegment(sketch, "E144", {"start": v(54.85, 41.25) * mm, "end": v(51.48, 39.35) * mm});
            skLineSegment(sketch, "E145", {"start": v(51.48, 39.35) * mm, "end": v(52.84, 36.93) * mm});
            skLineSegment(sketch, "E146", {"start": v(52.84, 36.93) * mm, "end": v(53.54, 37.32) * mm});
            skLineSegment(sketch, "E147", {"start": v(53.54, 37.32) * mm, "end": v(52.73, 38.75) * mm});
            skLineSegment(sketch, "E148", {"start": v(52.73, 38.75) * mm, "end": v(55.43, 40.28) * mm});
            skLineSegment(sketch, "E149", {"start": v(55.43, 40.28) * mm, "end": v(54.85, 41.25) * mm});
            skLineSegment(sketch, "E150", {"start": v(57.17, 36.1) * mm, "end": v(53.6, 35.06) * mm});
            skLineSegment(sketch, "E151", {"start": v(53.6, 35.06) * mm, "end": v(54, 33.27) * mm});
            skLineSegment(sketch, "E152", {"start": v(57.17, 36.1) * mm, "end": v(57.76, 34.05) * mm});
            skLineSegment(sketch, "E153", {"start": v(57.25, 32.57) * mm, "end": v(55.35, 32.12) * mm});
            skFitSpline(sketch, "E154", {"points": [v(57.76, 34.05) * mm, v(57.83, 33.45) * mm, v(57.65, 32.92) * mm, v(57.25, 32.57) * mm], "startDerivative": vector(0.33, -1.75) * mm, "endDerivative": vector(-1.37, -0.98) * mm});
            skFitSpline(sketch, "E155", {"points": [v(55.35, 32.12) * mm, v(54.74, 32.2) * mm, v(54.24, 32.63) * mm, v(54, 33.27) * mm], "startDerivative": vector(-1.94, 0.03) * mm, "endDerivative": vector(-0.54, 1.96) * mm});
            skLineSegment(sketch, "E156", {"start": v(56.54, 34.9) * mm, "end": v(54.61, 34.38) * mm});
            skLineSegment(sketch, "E157", {"start": v(54.61, 34.38) * mm, "end": v(54.93, 33.2) * mm});
            skLineSegment(sketch, "E158", {"start": v(54.93, 33.2) * mm, "end": v(56.84, 33.72) * mm});
            skLineSegment(sketch, "E159", {"start": v(56.84, 33.72) * mm, "end": v(56.54, 34.9) * mm});
            skLineSegment(sketch, "E160", {"start": v(57.42, 27.6) * mm, "end": v(57.42, 26.87) * mm});
            skLineSegment(sketch, "E161", {"start": v(55.78, 29.79) * mm, "end": v(55.78, 28.93) * mm});
            skLineSegment(sketch, "E162", {"start": v(55.78, 29.79) * mm, "end": v(55.14, 29.79) * mm});
            skPoint(sketch, "E163.1.internal.snap0", {"position": v(55.78, 29.36) * mm});
            skFitSpline(sketch, "E163", {"points": [v(55.14, 29.79) * mm, v(54.8, 29.36) * mm, v(54.57, 28.76) * mm, v(54.58, 27.7) * mm, v(54.65, 27.16) * mm, v(55.14, 26.68) * mm, v(56.08, 26.66) * mm, v(56.57, 26.93) * mm, v(56.87, 27.57) * mm, v(56.9, 28.46) * mm, v(56.91, 28.83) * mm, v(57.27, 28.95) * mm, v(57.68, 28.88) * mm, v(57.9, 28.44) * mm, v(57.87, 27.96) * mm, v(57.64, 27.6) * mm, v(57.42, 27.6) * mm], "startDerivative": vector(-5.78, -6.73) * mm, "endDerivative": vector(-5.74, 1.15) * mm});
            skFitSpline(sketch, "E164", {"points": [v(57.46, 26.87) * mm, v(58.07, 26.87) * mm, v(58.44, 27.45) * mm, v(58.56, 28.2) * mm, v(58.55, 28.95) * mm, v(58.26, 29.56) * mm, v(57.8, 29.79) * mm, v(57.02, 29.79) * mm, v(56.66, 29.66) * mm, v(56.28, 29.23) * mm], "startDerivative": vector(5.87, -1.17) * mm, "endDerivative": vector(-3.27, -4.4) * mm});
            skLineSegment(sketch, "E165", {"start": v(56.28, 29.23) * mm, "end": v(56.28, 27.92) * mm});
            skFitSpline(sketch, "E166", {"points": [v(56.28, 27.92) * mm, v(55.96, 27.66) * mm, v(55.45, 27.75) * mm, v(55.25, 28.13) * mm, v(55.27, 28.64) * mm, v(55.53, 28.9) * mm, v(55.78, 28.93) * mm], "startDerivative": vector(-1.56, -1.97) * mm, "endDerivative": vector(1.93, 0.04) * mm});
            skLineSegment(sketch, "E167", {"start": v(57.46, 26.87) * mm, "end": v(57.42, 26.87) * mm});
            skLineSegment(sketch, "E168", {"start": v(44.41, 6.82) * mm, "end": v(43.66, 6.46) * mm});
            skLineSegment(sketch, "E169", {"start": v(43.66, 6.46) * mm, "end": v(43.05, 7.73) * mm});
            skLineSegment(sketch, "E170", {"start": v(43.05, 7.73) * mm, "end": v(41.26, 6.88) * mm});
            skLineSegment(sketch, "E171", {"start": v(41.26, 6.88) * mm, "end": v(40.17, 9.14) * mm});
            skLineSegment(sketch, "E172", {"start": v(40.17, 9.14) * mm, "end": v(40.91, 9.5) * mm});
            skLineSegment(sketch, "E173", {"start": v(40.91, 9.5) * mm, "end": v(41.65, 7.96) * mm});
            skLineSegment(sketch, "E174", {"start": v(41.65, 7.96) * mm, "end": v(42.7, 8.46) * mm});
            skLineSegment(sketch, "E175", {"start": v(42.7, 8.46) * mm, "end": v(41.98, 9.94) * mm});
            skLineSegment(sketch, "E176", {"start": v(41.98, 9.94) * mm, "end": v(42.79, 10.33) * mm});
            skLineSegment(sketch, "E177", {"start": v(42.79, 10.33) * mm, "end": v(44.41, 6.82) * mm});
            skSolve(sketch);
        }
        {
            var Q0;
            Q0 = qSketchRegion(id + "F4", true);
            extrude(context, id + "F5", {"entities" : qUnion([Q0]), "operationType" : NewBodyOperationType.ADD, "depth" : 5 * mm, "offsetDistance" : 25 * mm});
        }
        {
            var Q0;
            Q0=makeQuery(id+"F3.boolean.opBoolean","SPLIT",FACE,{"disambiguationData":[TD([makeQuery(id+"F3.opExtrude","SWEPT_FACE",FACE,{"disambiguationData":[OSD([sQuery(id+"F2.wireOp",EDGE,"E9")])]})])],"derivedFrom":makeQuery(id+"F1.opExtrude","CAP_FACE",FACE,{"disambiguationData":[OSD([sQuery(id+"F0.wireOp",EDGE,"E0"),sQuery(id+"F0.wireOp",EDGE,"E1"),sQuery(id+"F0.wireOp",EDGE,"E2")])],"isStart":false})});
            var sketch = newSketch(context, id + "F6", { "sketchPlane" : qUnion([Q0])});
            skFitSpline(sketch, "E178", {"points": [v(33.09, 46.82) * mm, v(30.43, 46.64) * mm, v(27.48, 45.58) * mm, v(24.25, 43.85) * mm, v(21.6, 41.54) * mm, v(19.16, 38.53) * mm, v(17.47, 35.15) * mm, v(16.77, 32.85) * mm, v(16.34, 30.17) * mm, v(16.16, 27.59) * mm, v(16.67, 24.81) * mm, v(17.24, 22.93) * mm, v(18.18, 21.34) * mm, v(19.54, 20.07) * mm, v(21.89, 19.4) * mm, v(25.04, 20.2) * mm, v(27.76, 21.9) * mm, v(29.64, 23.4) * mm, v(30.78, 24.48) * mm, v(31, 24.7) * mm], "startDerivative": vector(-46.85, 6.54) * mm, "endDerivative": vector(9.8, 9.87) * mm});
            skLineSegment(sketch, "E179", {"start": v(31, 24.7) * mm, "end": v(30.27, 25.3) * mm});
            skFitSpline(sketch, "E180", {"points": [v(30.27, 25.3) * mm, v(29.17, 24.34) * mm, v(27.31, 22.76) * mm, v(25.5, 21.64) * mm, v(24.33, 21.1) * mm, v(22.64, 20.5) * mm, v(20.69, 20.6) * mm, v(18.95, 21.96) * mm, v(17.99, 23.91) * mm, v(17.45, 25.65) * mm, v(17.05, 27.53) * mm, v(16.98, 29.06) * mm, v(17.14, 30.82) * mm, v(17.78, 33.4) * mm, v(18.97, 36.32) * mm, v(20.22, 38.55) * mm, v(21.75, 40.29) * mm, v(23.79, 42.29) * mm, v(25.5, 43.48) * mm, v(28.42, 44.82) * mm, v(30.27, 45.55) * mm, v(31.85, 45.88) * mm, v(33.05, 45.9) * mm], "startDerivative": vector(-26.98, -23.17) * mm, "endDerivative": vector(33.35, -0.8) * mm});
            skFitSpline(sketch, "E181", {"points": [v(33.05, 45.9) * mm, v(32.7, 44.68) * mm, v(32.55, 43.06) * mm, v(32.52, 42.17) * mm], "startDerivative": vector(-1.22, -3.54) * mm, "endDerivative": vector(0.33, -3.46) * mm});
            skFitSpline(sketch, "E182", {"points": [v(51.5, 27.37) * mm, v(51.5, 26.35) * mm, v(50.72, 23.4) * mm, v(49.62, 20.52) * mm, v(47.52, 17.48) * mm, v(45.47, 15.39) * mm, v(42.43, 13.37) * mm, v(39.27, 11.95) * mm, v(35.83, 11.48) * mm, v(34.36, 11.45) * mm, v(31.96, 11.92) * mm, v(30.09, 13.05) * mm, v(29.42, 14.23) * mm, v(29.39, 15.77) * mm, v(29.82, 17.62) * mm, v(30.82, 19.71) * mm, v(31.9, 21.34) * mm, v(32.76, 22.73) * mm, v(32.98, 23.06) * mm], "startDerivative": vector(2.6, -25.99) * mm, "endDerivative": vector(7.96, 11.15) * mm});
            skLineSegment(sketch, "E183", {"start": v(32.98, 23.06) * mm, "end": v(32.34, 23.6) * mm});
            skFitSpline(sketch, "E184", {"points": [v(32.34, 23.6) * mm, v(31.88, 23.06) * mm, v(31.46, 22.53) * mm, v(31.12, 22.05) * mm, v(30.78, 21.52) * mm, v(30.24, 20.73) * mm, v(29.57, 19.6) * mm, v(28.94, 18.3) * mm, v(28.43, 16.67) * mm, v(28.32, 14.33) * mm, v(28.64, 13.25) * mm, v(29.9, 11.91) * mm, v(31.2, 11.11) * mm, v(33, 10.62) * mm, v(35.46, 10.5) * mm, v(37.7, 10.71) * mm, v(40.33, 11.4) * mm, v(43.27, 12.7) * mm, v(45.35, 14.06) * mm, v(47.52, 15.94) * mm, v(49.16, 17.82) * mm, v(50.18, 19.4) * mm, v(51.23, 21.43) * mm, v(51.9, 23.46) * mm, v(52.2, 24.56) * mm, v(52.5, 26.25) * mm, v(52.58, 27.21) * mm, v(52.56, 28.84) * mm, v(52.54, 30.6) * mm, v(51.9, 33.54) * mm, v(51.15, 35.65) * mm, v(49.8, 38.03) * mm, v(48.35, 40.2) * mm, v(46.3, 42.38) * mm, v(44.24, 43.86) * mm, v(42.52, 44.94) * mm, v(40, 45.99) * mm, v(38.03, 46.6) * mm, v(35.32, 46.8) * mm, v(33.09, 46.82) * mm], "startDerivative": vector(-29.64, -34.05) * mm, "endDerivative": vector(-75, 1.04) * mm});
            skLineSegment(sketch, "E185", {"start": v(30.27, 25.3) * mm, "end": v(30.27, 25.67) * mm});
            skLineSegment(sketch, "E186", {"start": v(30.27, 25.67) * mm, "end": v(27.2, 28.15) * mm});
            skLineSegment(sketch, "E187", {"start": v(27.2, 28.15) * mm, "end": v(28.4, 29.63) * mm});
            skLineSegment(sketch, "E188", {"start": v(28.4, 29.63) * mm, "end": v(34.58, 30.46) * mm});
            skLineSegment(sketch, "E189", {"start": v(34.58, 30.46) * mm, "end": v(37.4, 28.17) * mm});
            skLineSegment(sketch, "E190", {"start": v(37.4, 28.17) * mm, "end": v(37.75, 21.93) * mm});
            skLineSegment(sketch, "E191", {"start": v(37.75, 21.93) * mm, "end": v(36.64, 20.55) * mm});
            skLineSegment(sketch, "E192", {"start": v(36.64, 20.55) * mm, "end": v(33.37, 23.2) * mm});
            skLineSegment(sketch, "E193", {"start": v(33.37, 23.2) * mm, "end": v(32.98, 23.06) * mm});
            skLineSegment(sketch, "E194", {"start": v(32.34, 23.6) * mm, "end": v(31, 24.7) * mm});
            skFitSpline(sketch, "E195", {"points": [v(32.52, 42.17) * mm, v(31.6, 41.69) * mm, v(30.71, 41.15) * mm, v(29.92, 40.67) * mm, v(29.11, 40.07) * mm, v(28.2, 39.32) * mm, v(27.47, 38.69) * mm, v(26.9, 38.14) * mm, v(26.33, 37.34) * mm, v(25.98, 36.64) * mm, v(25.92, 35.96) * mm, v(25.93, 35.29) * mm, v(26.09, 34.66) * mm, v(26.52, 34.15) * mm, v(27.2, 33.5) * mm, v(28.27, 32.96) * mm, v(29.14, 32.6) * mm, v(30.4, 32.32) * mm, v(31.53, 32.19) * mm, v(32.66, 32.14) * mm, v(34.43, 32.1) * mm, v(36.13, 32.18) * mm], "startDerivative": vector(-19.14, -9.53) * mm, "endDerivative": vector(27.3, 2.76) * mm});
            skFitSpline(sketch, "E196", {"points": [v(36.13, 32.18) * mm, v(36.76, 31.54) * mm, v(37.55, 30.86) * mm, v(38.94, 29.76) * mm, v(40.38, 28.75) * mm, v(41.58, 28.1) * mm, v(43.3, 27.42) * mm, v(45.1, 27) * mm, v(46.51, 26.73) * mm, v(48.04, 26.78) * mm, v(50.37, 27.11) * mm, v(51.5, 27.37) * mm], "startDerivative": vector(8.05, -10.67) * mm, "endDerivative": vector(12.83, 3.86) * mm});
            skFitSpline(sketch, "E197", {"points": [v(32.52, 40.82) * mm, v(31.5, 40.07) * mm, v(29.37, 38.34) * mm, v(28.54, 37.33) * mm, v(28.24, 36.44) * mm, v(28.3, 35.2) * mm, v(29.45, 34.38) * mm, v(31.2, 33.85) * mm, v(33.72, 33.5) * mm, v(35.28, 33.52) * mm], "startDerivative": vector(-8.97, -6.52) * mm, "endDerivative": vector(13.14, 0.73) * mm});
            skFitSpline(sketch, "E198", {"points": [v(35.28, 33.52) * mm, v(34.46, 34.76) * mm, v(33.48, 36.83) * mm, v(33.03, 37.79) * mm, v(32.65, 39.2) * mm, v(32.52, 40.82) * mm], "startDerivative": vector(-4.08, 5.65) * mm, "endDerivative": vector(-1.34, 5.1) * mm});
            skLineSegment(sketch, "E199", {"start": v(34.56, 29.15) * mm, "end": v(36.12, 27.9) * mm});
            skLineSegment(sketch, "E200", {"start": v(36.12, 27.9) * mm, "end": v(35.39, 27) * mm});
            skLineSegment(sketch, "E201", {"start": v(35.39, 27) * mm, "end": v(33.82, 28.27) * mm});
            skLineSegment(sketch, "E202", {"start": v(33.82, 28.27) * mm, "end": v(34.56, 29.15) * mm});
            skSolve(sketch);
        }
        {
            var Q0;
            Q0 = qSketchRegion(id + "F6", true);
            extrude(context, id + "F7", {"entities" : qUnion([Q0]), "operationType" : NewBodyOperationType.ADD, "depth" : 5 * mm, "offsetDistance" : 25 * mm});
        }
        {
            var Q0;
            Q0=makeQuery(id+"F7.boolean.opBoolean","SPLIT",FACE,{"disambiguationData":[TD([makeQuery(id+"F7.opExtrude","SWEPT_FACE",FACE,{"disambiguationData":[OSD([sQuery(id+"F6.wireOp",EDGE,"E180")])]})])],"derivedFrom":makeQuery(id+"F3.boolean.opBoolean","SPLIT",FACE,{"disambiguationData":[TD([makeQuery(id+"F3.opExtrude","SWEPT_FACE",FACE,{"disambiguationData":[OSD([sQuery(id+"F2.wireOp",EDGE,"E9")])]})])],"derivedFrom":makeQuery(id+"F1.opExtrude","CAP_FACE",FACE,{"disambiguationData":[OSD([sQuery(id+"F0.wireOp",EDGE,"E0"),sQuery(id+"F0.wireOp",EDGE,"E1"),sQuery(id+"F0.wireOp",EDGE,"E2")])],"isStart":false})})});
            var sketch = newSketch(context, id + "F8", { "sketchPlane" : qUnion([Q0])});
            skArc(sketch, "E203", {"start": v(20.98, 30.62) * mm, "mid": v(22.14, 31.17) * mm, "end": v(22.9, 32.2) * mm});
            skArc(sketch, "E204", {"start": v(23.7, 32.2) * mm, "mid": v(24.33, 31.1) * mm, "end": v(25.52, 30.62) * mm});
            skArc(sketch, "E205", {"start": v(22.9, 28.13) * mm, "mid": v(22.26, 29.4) * mm, "end": v(20.98, 30.01) * mm});
            skArc(sketch, "E206", {"start": v(25.52, 29.91) * mm, "mid": v(24.29, 29.47) * mm, "end": v(23.7, 28.3) * mm});
            skLineSegment(sketch, "E207", {"start": v(22.9, 28.13) * mm, "end": v(23.26, 25.97) * mm});
            skLineSegment(sketch, "E208", {"start": v(23.26, 25.97) * mm, "end": v(23.7, 28.3) * mm});
            skLineSegment(sketch, "E209", {"start": v(20.98, 30.01) * mm, "end": v(18.96, 30.25) * mm});
            skLineSegment(sketch, "E210", {"start": v(18.96, 30.25) * mm, "end": v(20.98, 30.62) * mm});
            skLineSegment(sketch, "E211", {"start": v(25.52, 29.91) * mm, "end": v(27.45, 30.24) * mm});
            skLineSegment(sketch, "E212", {"start": v(27.45, 30.24) * mm, "end": v(25.52, 30.62) * mm});
            skLineSegment(sketch, "E213", {"start": v(23.7, 32.2) * mm, "end": v(23.24, 34.9) * mm});
            skLineSegment(sketch, "E214", {"start": v(23.24, 34.9) * mm, "end": v(22.9, 32.2) * mm});
            skArc(sketch, "E215", {"start": v(40.2, 19.69) * mm, "mid": v(40.54, 19.96) * mm, "end": v(40.75, 20.35) * mm});
            skArc(sketch, "E216", {"start": v(41.46, 20.35) * mm, "mid": v(41.61, 19.96) * mm, "end": v(41.93, 19.69) * mm});
            skArc(sketch, "E217", {"start": v(41.93, 18.98) * mm, "mid": v(41.6, 18.58) * mm, "end": v(41.46, 18.07) * mm});
            skArc(sketch, "E218", {"start": v(40.75, 18.07) * mm, "mid": v(40.6, 18.6) * mm, "end": v(40.2, 18.98) * mm});
            skLineSegment(sketch, "E219", {"start": v(40.2, 18.98) * mm, "end": v(38.78, 19.3) * mm});
            skLineSegment(sketch, "E220", {"start": v(38.78, 19.3) * mm, "end": v(40.2, 19.69) * mm});
            skLineSegment(sketch, "E221", {"start": v(40.75, 18.07) * mm, "end": v(41.1, 16.83) * mm});
            skLineSegment(sketch, "E222", {"start": v(41.1, 16.83) * mm, "end": v(41.46, 18.07) * mm});
            skLineSegment(sketch, "E223", {"start": v(41.93, 18.98) * mm, "end": v(43.22, 19.22) * mm});
            skLineSegment(sketch, "E224", {"start": v(41.93, 19.69) * mm, "end": v(43.22, 19.22) * mm});
            skLineSegment(sketch, "E225", {"start": v(41.46, 20.35) * mm, "end": v(41.17, 21.87) * mm});
            skLineSegment(sketch, "E226", {"start": v(41.17, 21.87) * mm, "end": v(40.75, 20.35) * mm});
            skArc(sketch, "E227", {"start": v(24.9, 39.85) * mm, "mid": v(25.05, 39.98) * mm, "end": v(25.12, 40.16) * mm});
            skArc(sketch, "E228", {"start": v(25.53, 40.16) * mm, "mid": v(25.59, 39.98) * mm, "end": v(25.72, 39.85) * mm});
            skArc(sketch, "E229", {"start": v(25.72, 39.59) * mm, "mid": v(25.6, 39.5) * mm, "end": v(25.53, 39.36) * mm});
            skArc(sketch, "E230", {"start": v(25.12, 39.36) * mm, "mid": v(25.05, 39.51) * mm, "end": v(24.9, 39.6) * mm});
            skLineSegment(sketch, "E231", {"start": v(25.12, 39.36) * mm, "end": v(25.29, 38.73) * mm});
            skLineSegment(sketch, "E232", {"start": v(25.29, 38.73) * mm, "end": v(25.53, 39.36) * mm});
            skLineSegment(sketch, "E233", {"start": v(25.72, 39.59) * mm, "end": v(26.27, 39.7) * mm});
            skLineSegment(sketch, "E234", {"start": v(26.27, 39.7) * mm, "end": v(25.72, 39.85) * mm});
            skLineSegment(sketch, "E235", {"start": v(25.53, 40.16) * mm, "end": v(25.3, 40.79) * mm});
            skLineSegment(sketch, "E236", {"start": v(25.3, 40.79) * mm, "end": v(25.12, 40.16) * mm});
            skLineSegment(sketch, "E237", {"start": v(24.9, 39.85) * mm, "end": v(24.33, 39.74) * mm});
            skLineSegment(sketch, "E238", {"start": v(24.33, 39.74) * mm, "end": v(24.9, 39.6) * mm});
            skArc(sketch, "E239", {"start": v(30.62, 35.9) * mm, "mid": v(30.74, 36.06) * mm, "end": v(30.82, 36.25) * mm});
            skArc(sketch, "E240", {"start": v(31.18, 36.25) * mm, "mid": v(31.25, 36.06) * mm, "end": v(31.38, 35.9) * mm});
            skArc(sketch, "E241", {"start": v(31.38, 35.58) * mm, "mid": v(31.24, 35.46) * mm, "end": v(31.18, 35.28) * mm});
            skArc(sketch, "E242", {"start": v(30.83, 35.28) * mm, "mid": v(30.77, 35.48) * mm, "end": v(30.62, 35.62) * mm});
            skLineSegment(sketch, "E243", {"start": v(30.83, 35.28) * mm, "end": v(31, 34.6) * mm});
            skLineSegment(sketch, "E244", {"start": v(31, 34.6) * mm, "end": v(31.18, 35.28) * mm});
            skLineSegment(sketch, "E245", {"start": v(31.38, 35.58) * mm, "end": v(31.95, 35.65) * mm});
            skLineSegment(sketch, "E246", {"start": v(31.95, 35.65) * mm, "end": v(31.38, 35.9) * mm});
            skLineSegment(sketch, "E247", {"start": v(31.18, 36.25) * mm, "end": v(31.04, 36.8) * mm});
            skLineSegment(sketch, "E248", {"start": v(31.04, 36.8) * mm, "end": v(30.82, 36.25) * mm});
            skLineSegment(sketch, "E249", {"start": v(30.62, 35.9) * mm, "end": v(30.05, 35.76) * mm});
            skLineSegment(sketch, "E250", {"start": v(30.05, 35.76) * mm, "end": v(30.62, 35.62) * mm});
            skArc(sketch, "E251", {"start": v(19.85, 35.05) * mm, "mid": v(20.2, 35.29) * mm, "end": v(20.27, 35.7) * mm});
            skArc(sketch, "E252", {"start": v(20.77, 35.7) * mm, "mid": v(20.8, 35.3) * mm, "end": v(21.13, 35.05) * mm});
            skArc(sketch, "E253", {"start": v(21.13, 34.72) * mm, "mid": v(20.82, 34.46) * mm, "end": v(20.77, 34.06) * mm});
            skArc(sketch, "E254", {"start": v(20.27, 34.06) * mm, "mid": v(20.18, 34.46) * mm, "end": v(19.85, 34.7) * mm});
            skLineSegment(sketch, "E255", {"start": v(20.27, 34.06) * mm, "end": v(20.52, 33.13) * mm});
            skLineSegment(sketch, "E256", {"start": v(20.77, 34.06) * mm, "end": v(20.52, 33.13) * mm});
            skLineSegment(sketch, "E257", {"start": v(19.85, 34.7) * mm, "end": v(19.2, 34.86) * mm});
            skLineSegment(sketch, "E258", {"start": v(19.2, 34.86) * mm, "end": v(19.85, 35.05) * mm});
            skLineSegment(sketch, "E259", {"start": v(20.27, 35.7) * mm, "end": v(20.52, 36.5) * mm});
            skLineSegment(sketch, "E260", {"start": v(20.52, 36.5) * mm, "end": v(20.77, 35.7) * mm});
            skLineSegment(sketch, "E261", {"start": v(21.13, 35.05) * mm, "end": v(21.93, 34.86) * mm});
            skLineSegment(sketch, "E262", {"start": v(21.93, 34.86) * mm, "end": v(21.13, 34.72) * mm});
            skArc(sketch, "E263", {"start": v(19.56, 26.94) * mm, "mid": v(19.73, 27.07) * mm, "end": v(19.8, 27.27) * mm});
            skArc(sketch, "E264", {"start": v(20.17, 27.27) * mm, "mid": v(20.26, 27.07) * mm, "end": v(20.43, 26.94) * mm});
            skArc(sketch, "E265", {"start": v(20.43, 26.63) * mm, "mid": v(20.26, 26.47) * mm, "end": v(20.17, 26.26) * mm});
            skArc(sketch, "E266", {"start": v(19.8, 26.26) * mm, "mid": v(19.74, 26.49) * mm, "end": v(19.56, 26.64) * mm});
            skLineSegment(sketch, "E267", {"start": v(19.8, 26.26) * mm, "end": v(19.96, 25.52) * mm});
            skLineSegment(sketch, "E268", {"start": v(19.96, 25.52) * mm, "end": v(20.17, 26.26) * mm});
            skLineSegment(sketch, "E269", {"start": v(20.43, 26.63) * mm, "end": v(21.12, 26.77) * mm});
            skLineSegment(sketch, "E270", {"start": v(21.12, 26.77) * mm, "end": v(20.43, 26.94) * mm});
            skLineSegment(sketch, "E271", {"start": v(20.17, 27.27) * mm, "end": v(19.98, 27.92) * mm});
            skLineSegment(sketch, "E272", {"start": v(19.98, 27.92) * mm, "end": v(19.8, 27.27) * mm});
            skLineSegment(sketch, "E273", {"start": v(19.56, 26.64) * mm, "end": v(18.87, 26.77) * mm});
            skLineSegment(sketch, "E274", {"start": v(18.87, 26.77) * mm, "end": v(19.56, 26.94) * mm});
            skArc(sketch, "E275", {"start": v(46.91, 21.91) * mm, "mid": v(47.08, 22.1) * mm, "end": v(47.17, 22.33) * mm});
            skArc(sketch, "E276", {"start": v(47.53, 22.33) * mm, "mid": v(47.6, 22.1) * mm, "end": v(47.77, 21.91) * mm});
            skArc(sketch, "E277", {"start": v(47.77, 21.62) * mm, "mid": v(47.6, 21.48) * mm, "end": v(47.53, 21.27) * mm});
            skArc(sketch, "E278", {"start": v(47.23, 21.27) * mm, "mid": v(47.14, 21.51) * mm, "end": v(46.91, 21.64) * mm});
            skLineSegment(sketch, "E279", {"start": v(47.23, 21.27) * mm, "end": v(47.35, 20.63) * mm});
            skLineSegment(sketch, "E280", {"start": v(47.35, 20.63) * mm, "end": v(47.53, 21.27) * mm});
            skLineSegment(sketch, "E281", {"start": v(47.77, 21.62) * mm, "end": v(48.43, 21.77) * mm});
            skLineSegment(sketch, "E282", {"start": v(48.43, 21.77) * mm, "end": v(47.77, 21.91) * mm});
            skLineSegment(sketch, "E283", {"start": v(47.53, 22.33) * mm, "end": v(47.34, 22.88) * mm});
            skLineSegment(sketch, "E284", {"start": v(47.34, 22.88) * mm, "end": v(47.17, 22.33) * mm});
            skLineSegment(sketch, "E285", {"start": v(46.91, 21.64) * mm, "end": v(46.29, 21.75) * mm});
            skLineSegment(sketch, "E286", {"start": v(46.29, 21.75) * mm, "end": v(46.91, 21.91) * mm});
            skArc(sketch, "E287", {"start": v(34.56, 14.61) * mm, "mid": v(34.79, 14.76) * mm, "end": v(34.83, 15.02) * mm});
            skArc(sketch, "E288", {"start": v(34.86, 13.9) * mm, "mid": v(34.78, 14.18) * mm, "end": v(34.56, 14.37) * mm});
            skArc(sketch, "E289", {"start": v(35.45, 14.37) * mm, "mid": v(35.26, 14.18) * mm, "end": v(35.19, 13.9) * mm});
            skArc(sketch, "E290", {"start": v(35.2, 15.02) * mm, "mid": v(35.27, 14.79) * mm, "end": v(35.45, 14.61) * mm});
            skLineSegment(sketch, "E291", {"start": v(34.83, 15.02) * mm, "end": v(35.04, 15.66) * mm});
            skLineSegment(sketch, "E292", {"start": v(35.04, 15.66) * mm, "end": v(35.2, 15.02) * mm});
            skLineSegment(sketch, "E293", {"start": v(35.45, 14.61) * mm, "end": v(36.07, 14.5) * mm});
            skLineSegment(sketch, "E294", {"start": v(36.07, 14.5) * mm, "end": v(35.45, 14.37) * mm});
            skLineSegment(sketch, "E295", {"start": v(35.19, 13.9) * mm, "end": v(35.08, 13.28) * mm});
            skLineSegment(sketch, "E296", {"start": v(35.08, 13.28) * mm, "end": v(34.86, 13.9) * mm});
            skLineSegment(sketch, "E297", {"start": v(34.56, 14.37) * mm, "end": v(33.93, 14.5) * mm});
            skLineSegment(sketch, "E298", {"start": v(33.93, 14.5) * mm, "end": v(34.56, 14.61) * mm});
            skArc(sketch, "E299", {"start": v(32.66, 17.98) * mm, "mid": v(32.85, 18.1) * mm, "end": v(32.93, 18.3) * mm});
            skArc(sketch, "E300", {"start": v(33.38, 18.3) * mm, "mid": v(33.45, 18.09) * mm, "end": v(33.65, 17.98) * mm});
            skArc(sketch, "E301", {"start": v(33.65, 17.72) * mm, "mid": v(33.44, 17.64) * mm, "end": v(33.38, 17.42) * mm});
            skArc(sketch, "E302", {"start": v(32.93, 17.42) * mm, "mid": v(32.86, 17.64) * mm, "end": v(32.66, 17.75) * mm});
            skLineSegment(sketch, "E303", {"start": v(32.93, 17.42) * mm, "end": v(33.1, 16.59) * mm});
            skLineSegment(sketch, "E304", {"start": v(33.1, 16.59) * mm, "end": v(33.38, 17.42) * mm});
            skLineSegment(sketch, "E305", {"start": v(33.65, 17.72) * mm, "end": v(34.18, 17.79) * mm});
            skLineSegment(sketch, "E306", {"start": v(34.18, 17.79) * mm, "end": v(33.65, 17.98) * mm});
            skLineSegment(sketch, "E307", {"start": v(33.38, 18.3) * mm, "end": v(33.13, 19) * mm});
            skLineSegment(sketch, "E308", {"start": v(33.13, 19) * mm, "end": v(32.93, 18.3) * mm});
            skLineSegment(sketch, "E309", {"start": v(32.66, 17.75) * mm, "end": v(32.03, 17.8) * mm});
            skLineSegment(sketch, "E310", {"start": v(32.03, 17.8) * mm, "end": v(32.66, 17.98) * mm});
            skSolve(sketch);
        }
        {
            var Q0;
            Q0 = qSketchRegion(id + "F8", true);
            extrude(context, id + "F9", {"entities" : qUnion([Q0]), "operationType" : NewBodyOperationType.ADD, "depth" : 5 * mm, "offsetDistance" : 25 * mm});
        }
    });
